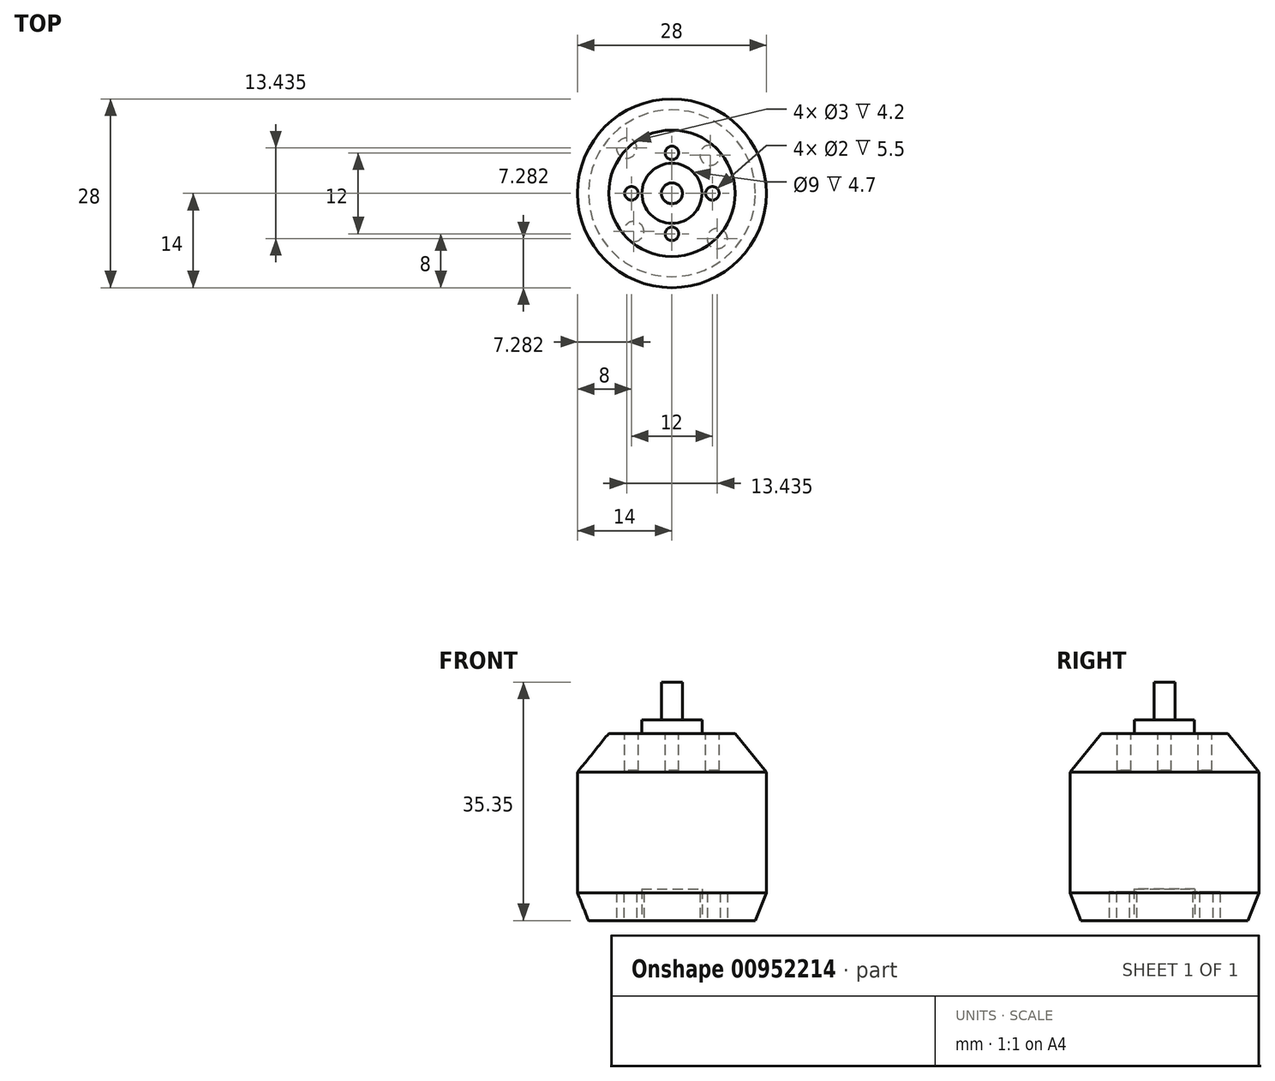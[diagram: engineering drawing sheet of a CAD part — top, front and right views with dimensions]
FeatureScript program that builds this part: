
annotation { "Feature Type Name" : "Feature", "Feature Type Description" : "" }
export const myFeature = defineFeature(function(context is Context, id is Id, definition is map)
    precondition{}
    {
        {
            var Q0;
            Q0=qCreatedBy(makeId("Top.planeOp"),FACE);
            var sketch = newSketch(context, id + "F0", { "sketchPlane" : qUnion([Q0])});
            skCircle(sketch, "E0", {"center": v(0, 0) * mm, "radius": 14 * mm});
            skSolve(sketch);
        }
        {
            var Q0;
            Q0 = qSketchRegion(id + "F0", true);
            extrude(context, id + "F1", {"entities" : qUnion([Q0]), "depth" : 27.75 * mm, "offsetDistance" : 25 * mm});
        }
        {
            var Q0;
            Q0=makeQuery(id+"F1.opExtrude","CAP_FACE",FACE,{"disambiguationData":[OSD([sQuery(id+"F0.wireOp",EDGE,"E0")])],"isStart":false});
            var sketch = newSketch(context, id + "F2", { "sketchPlane" : qUnion([Q0])});
            skCircle(sketch, "E1", {"center": v(0, 0) * mm, "radius": 9.38 * mm});
            skSolve(sketch);
        }
        {
            var Q0;
            Q0=qCreatedBy(makeId("Front.planeOp"),FACE);
            var sketch = newSketch(context, id + "F3", { "sketchPlane" : qUnion([Q0])});
            skLineSegment(sketch, "E2.0", {"start": v(-9.38, 27.75) * mm, "end": v(9.38, 27.75) * mm});
            skLineSegment(sketch, "E3", {"start": v(14, 27.75) * mm, "end": v(14, 0) * mm, "construction": true});
            skLineSegment(sketch, "E4", {"start": v(9.38, 27.75) * mm, "end": v(14, 22) * mm});
            skLineSegment(sketch, "E5", {"start": v(9.38, 27.75) * mm, "end": v(14, 27.75) * mm});
            skLineSegment(sketch, "E6", {"start": v(14, 27.75) * mm, "end": v(14, 22) * mm});
            skLineSegment(sketch, "E7", {"start": v(0, 27.75) * mm, "end": v(0, 0) * mm, "construction": true});
            skSolve(sketch);
        }
        {
            var Q0;
            Q0 = qSketchRegion(id + "F3", true);
            var Q1;
            Q1=sQuery(id+"F3.wireOp",EDGE,"E7");
            revolve(context, id + "F4", {"operationType" : NewBodyOperationType.REMOVE, "surfaceOperationType" : NewSurfaceOperationType.NEW, "entities" : qUnion([Q0]), "axis" : qUnion([Q1]), "revolveType" : RevolveType.FULL, "oppositeDirection" : true});
        }
        {
            var Q0;
            Q0=makeQuery(id+"F1.opExtrude","CAP_FACE",FACE,{"disambiguationData":[OSD([sQuery(id+"F0.wireOp",EDGE,"E0")])],"isStart":false});
            var sketch = newSketch(context, id + "F5", { "sketchPlane" : qUnion([Q0])});
            skCircle(sketch, "E8", {"center": v(0, 0) * mm, "radius": 4.45 * mm});
            skSolve(sketch);
        }
        {
            var Q0;
            Q0 = qSketchRegion(id + "F5", true);
            extrude(context, id + "F6", {"entities" : qUnion([Q0]), "operationType" : NewBodyOperationType.ADD, "depth" : 2 * mm, "offsetDistance" : 25 * mm});
        }
        {
            var Q0;
            Q0=makeQuery(id+"F6.opExtrude","CAP_FACE",FACE,{"disambiguationData":[OSD([sQuery(id+"F5.wireOp",EDGE,"E8")])],"isStart":false});
            var sketch = newSketch(context, id + "F7", { "sketchPlane" : qUnion([Q0])});
            skCircle(sketch, "E9", {"center": v(0, 0) * mm, "radius": 1.55 * mm});
            skSolve(sketch);
        }
        {
            var Q0;
            Q0 = qSketchRegion(id + "F7", true);
            extrude(context, id + "F8", {"entities" : qUnion([Q0]), "operationType" : NewBodyOperationType.ADD, "depth" : 5.6 * mm, "offsetDistance" : 25 * mm});
        }
        {
            var Q0;
            Q0=makeQuery(id+"F1.opExtrude","CAP_FACE",FACE,{"disambiguationData":[OSD([sQuery(id+"F0.wireOp",EDGE,"E0")])],"isStart":true});
            var sketch = newSketch(context, id + "F9", { "sketchPlane" : qUnion([Q0])});
            skCircle(sketch, "E10", {"center": v(0, 0) * mm, "radius": 12.38 * mm});
            skCircle(sketch, "E11", {"center": v(0, 0) * mm, "radius": 4.5 * mm});
            skSolve(sketch);
        }
        {
            var Q0;
            Q0=qCreatedBy(makeId("Front.planeOp"),FACE);
            var sketch = newSketch(context, id + "F10", { "sketchPlane" : qUnion([Q0])});
            skLineSegment(sketch, "E12.0.0", {"start": v(12.38, 0) * mm, "end": v(-12.38, 0) * mm});
            skLineSegment(sketch, "E13", {"start": v(14, 22) * mm, "end": v(14, 0) * mm});
            skLineSegment(sketch, "E14", {"start": v(12.38, 0) * mm, "end": v(14, 0) * mm});
            skLineSegment(sketch, "E15", {"start": v(14, 0) * mm, "end": v(14, 4.1) * mm});
            skLineSegment(sketch, "E16", {"start": v(14, 4.1) * mm, "end": v(12.37, 0) * mm});
            skLineSegment(sketch, "E17", {"start": v(14, 4.1) * mm, "end": v(14, 0) * mm});
            skSolve(sketch);
        }
        {
            var Q0;
            Q0 = qSketchRegion(id + "F10", true);
            var Q1;
            Q1=sQuery(id+"F3.wireOp",EDGE,"E7");
            revolve(context, id + "F11", {"operationType" : NewBodyOperationType.REMOVE, "surfaceOperationType" : NewSurfaceOperationType.NEW, "entities" : qUnion([Q0]), "axis" : qUnion([Q1]), "revolveType" : RevolveType.FULL, "oppositeDirection" : true});
        }
        {
            var Q0;
            Q0=makeQuery(id+"F9.imprint","IMPRINT",FACE,{"disambiguationData":[TD([[makeQuery(id+"F9.imprint","IMPRINT",EDGE,{"derivedFrom":sQuery(id+"F9.wireOp",EDGE,"E11")}),1.0]])]});
            extrude(context, id + "F12", {"entities" : qUnion([Q0]), "operationType" : NewBodyOperationType.REMOVE, "oppositeDirection" : true, "depth" : 4.7 * mm, "offsetDistance" : 25 * mm});
        }
        {
            var Q0;
            Q0=makeQuery(id+"F1.opExtrude","CAP_FACE",FACE,{"disambiguationData":[OSD([sQuery(id+"F0.wireOp",EDGE,"E0")])],"isStart":true});
            var sketch = newSketch(context, id + "F13", { "sketchPlane" : qUnion([Q0])});
            skLineSegment(sketch, "E18", {"start": v(-5.66, 5.66) * mm, "end": v(5.66, -5.66) * mm, "construction": true});
            skLineSegment(sketch, "E19", {"start": v(-6.72, -6.72) * mm, "end": v(6.72, 6.72) * mm, "construction": true});
            skCircle(sketch, "E20", {"center": v(-5.66, 5.66) * mm, "radius": 1.5 * mm});
            skCircle(sketch, "E21", {"center": v(6.72, 6.72) * mm, "radius": 1.5 * mm});
            skCircle(sketch, "E22", {"center": v(5.66, -5.66) * mm, "radius": 1.5 * mm});
            skCircle(sketch, "E23", {"center": v(-6.72, -6.72) * mm, "radius": 1.5 * mm});
            skSolve(sketch);
        }
        {
            var Q0;
            Q0 = qSketchRegion(id + "F13", true);
            extrude(context, id + "F14", {"entities" : qUnion([Q0]), "operationType" : NewBodyOperationType.REMOVE, "oppositeDirection" : true, "depth" : 4.2 * mm, "offsetDistance" : 25 * mm});
        }
        {
            var Q0;
            Q0=makeQuery(id+"F1.opExtrude","CAP_FACE",FACE,{"disambiguationData":[OSD([sQuery(id+"F0.wireOp",EDGE,"E0")])],"isStart":false});
            var sketch = newSketch(context, id + "F15", { "sketchPlane" : qUnion([Q0])});
            skLineSegment(sketch, "E24", {"start": v(0, 0) * mm, "end": v(0, -6) * mm, "construction": true});
            skCircle(sketch, "E25", {"center": v(0, -6) * mm, "radius": 1 * mm});
            skCircle(sketch, "E26.1.0", {"center": v(6, 0) * mm, "radius": 1 * mm});
            skCircle(sketch, "E26.2.0", {"center": v(0, 6) * mm, "radius": 1 * mm});
            skCircle(sketch, "E26.3.0", {"center": v(-6, 0) * mm, "radius": 1 * mm});
            skPoint(sketch, "E26.center", {"position": v(0, 0) * mm});
            skSolve(sketch);
        }
        {
            var Q0;
            Q0 = qSketchRegion(id + "F15", true);
            extrude(context, id + "F16", {"entities" : qUnion([Q0]), "operationType" : NewBodyOperationType.REMOVE, "oppositeDirection" : true, "depth" : 5.5 * mm, "offsetDistance" : 25 * mm});
        }
    });
